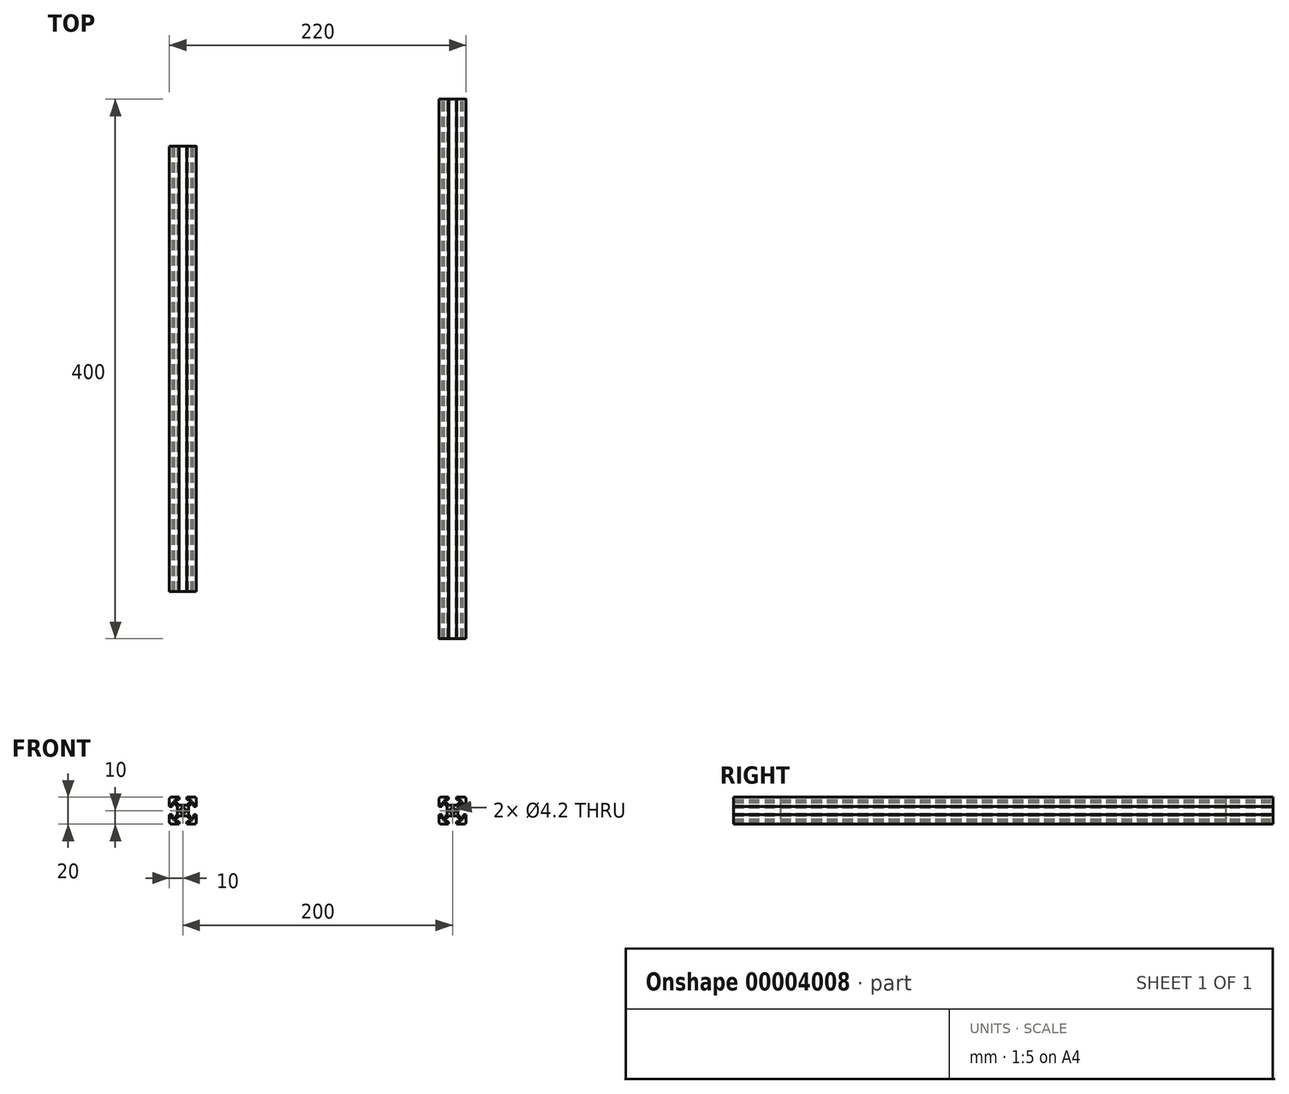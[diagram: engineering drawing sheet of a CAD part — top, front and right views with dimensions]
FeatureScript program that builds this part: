
annotation { "Feature Type Name" : "Feature", "Feature Type Description" : "" }
export const myFeature = defineFeature(function(context is Context, id is Id, definition is map)
    precondition{}
    {
        {
            var Q0;
            Q0=qCreatedBy(makeId("Front.planeOp"),FACE);
            var sketch = newSketch(context, id + "F0", { "sketchPlane" : qUnion([Q0])});
            skLineSegment(sketch, "E0", {"start": v(0, 0) * mm, "end": v(0, 4) * mm, "construction": true});
            skLineSegment(sketch, "E1", {"start": v(-2.94, 4) * mm, "end": v(2.94, 4) * mm});
            skLineSegment(sketch, "E2", {"start": v(0, 0) * mm, "end": v(10, 10) * mm, "construction": true});
            skLineSegment(sketch, "E3", {"start": v(10, 10) * mm, "end": v(-10, 10) * mm, "construction": true});
            skLineSegment(sketch, "E4", {"start": v(-10, 10) * mm, "end": v(0, 0) * mm, "construction": true});
            skLineSegment(sketch, "E5", {"start": v(-10, 10) * mm, "end": v(-3, 10) * mm});
            skLineSegment(sketch, "E6", {"start": v(-3, 10) * mm, "end": v(-3, 8) * mm});
            skLineSegment(sketch, "E7", {"start": v(-3, 8) * mm, "end": v(-6, 8) * mm});
            skLineSegment(sketch, "E8", {"start": v(-6, 8) * mm, "end": v(-6, 7.06) * mm});
            skLineSegment(sketch, "E9", {"start": v(-6, 7.06) * mm, "end": v(-2.94, 4) * mm});
            skLineSegment(sketch, "E10", {"start": v(2.94, 4) * mm, "end": v(6, 7.06) * mm});
            skLineSegment(sketch, "E11", {"start": v(6, 7.06) * mm, "end": v(6, 8) * mm});
            skLineSegment(sketch, "E12", {"start": v(6, 8) * mm, "end": v(3, 8) * mm});
            skLineSegment(sketch, "E13", {"start": v(3, 8) * mm, "end": v(3, 10) * mm});
            skLineSegment(sketch, "E14", {"start": v(3, 10) * mm, "end": v(10, 10) * mm});
            skLineSegment(sketch, "E15.0.MirrorCS", {"start": v(-10, -3) * mm, "end": v(-10, -10) * mm});
            skLineSegment(sketch, "E15.1.MirrorCS", {"start": v(-7.06, -6) * mm, "end": v(-8, -6) * mm});
            skLineSegment(sketch, "E15.2.MirrorCS", {"start": v(-8, -6) * mm, "end": v(-8, -3) * mm});
            skLineSegment(sketch, "E15.3.MirrorCS", {"start": v(-8, -3) * mm, "end": v(-10, -3) * mm});
            skLineSegment(sketch, "E15.4.MirrorCS", {"start": v(-10, 10) * mm, "end": v(-10, 3) * mm});
            skLineSegment(sketch, "E15.5.MirrorCS", {"start": v(-10, 3) * mm, "end": v(-8, 3) * mm});
            skLineSegment(sketch, "E15.6.MirrorCS", {"start": v(-8, 3) * mm, "end": v(-8, 6) * mm});
            skLineSegment(sketch, "E15.7.MirrorCS", {"start": v(-8, 6) * mm, "end": v(-7.06, 6) * mm});
            skLineSegment(sketch, "E15.8.MirrorCS", {"start": v(-7.06, 6) * mm, "end": v(-4, 2.94) * mm});
            skLineSegment(sketch, "E15.9.MirrorCS", {"start": v(-4, -2.94) * mm, "end": v(-7.06, -6) * mm});
            skLineSegment(sketch, "E15.10.MirrorCS", {"start": v(-4, 2.94) * mm, "end": v(-4, -2.94) * mm});
            skLineSegment(sketch, "E16", {"start": v(-10, -10) * mm, "end": v(0, 0) * mm, "construction": true});
            skLineSegment(sketch, "E17", {"start": v(-10, 10) * mm, "end": v(-10, -10) * mm, "construction": true});
            skLineSegment(sketch, "E18.0.MirrorCS", {"start": v(10, 3) * mm, "end": v(10, 10) * mm});
            skLineSegment(sketch, "E18.1.MirrorCS", {"start": v(8, 3) * mm, "end": v(10, 3) * mm});
            skLineSegment(sketch, "E18.2.MirrorCS", {"start": v(8, 6) * mm, "end": v(8, 3) * mm});
            skLineSegment(sketch, "E18.3.MirrorCS", {"start": v(7.06, 6) * mm, "end": v(8, 6) * mm});
            skLineSegment(sketch, "E18.4.MirrorCS", {"start": v(4, 2.94) * mm, "end": v(7.06, 6) * mm});
            skLineSegment(sketch, "E18.5.MirrorCS", {"start": v(4, -2.94) * mm, "end": v(4, 2.94) * mm});
            skLineSegment(sketch, "E18.6.MirrorCS", {"start": v(7.06, -6) * mm, "end": v(4, -2.94) * mm});
            skLineSegment(sketch, "E18.7.MirrorCS", {"start": v(8, -6) * mm, "end": v(7.06, -6) * mm});
            skLineSegment(sketch, "E18.8.MirrorCS", {"start": v(8, -3) * mm, "end": v(8, -6) * mm});
            skLineSegment(sketch, "E18.9.MirrorCS", {"start": v(10, -3) * mm, "end": v(8, -3) * mm});
            skLineSegment(sketch, "E18.10.MirrorCS", {"start": v(10, -10) * mm, "end": v(10, -3) * mm});
            skLineSegment(sketch, "E18.11.MirrorCS", {"start": v(10, -10) * mm, "end": v(3, -10) * mm});
            skLineSegment(sketch, "E18.12.MirrorCS", {"start": v(3, -10) * mm, "end": v(3, -8) * mm});
            skLineSegment(sketch, "E18.13.MirrorCS", {"start": v(3, -8) * mm, "end": v(6, -8) * mm});
            skLineSegment(sketch, "E18.14.MirrorCS", {"start": v(6, -8) * mm, "end": v(6, -7.06) * mm});
            skLineSegment(sketch, "E18.15.MirrorCS", {"start": v(6, -7.06) * mm, "end": v(2.94, -4) * mm});
            skLineSegment(sketch, "E18.16.MirrorCS", {"start": v(2.94, -4) * mm, "end": v(-2.94, -4) * mm});
            skLineSegment(sketch, "E18.17.MirrorCS", {"start": v(-2.94, -4) * mm, "end": v(-6, -7.06) * mm});
            skLineSegment(sketch, "E18.18.MirrorCS", {"start": v(-6, -7.06) * mm, "end": v(-6, -8) * mm});
            skLineSegment(sketch, "E18.19.MirrorCS", {"start": v(-6, -8) * mm, "end": v(-3, -8) * mm});
            skLineSegment(sketch, "E18.20.MirrorCS", {"start": v(-3, -10) * mm, "end": v(-10, -10) * mm});
            skLineSegment(sketch, "E18.21.MirrorCS", {"start": v(-3, -8) * mm, "end": v(-3, -10) * mm});
            skLineSegment(sketch, "E19", {"start": v(0, 0) * mm, "end": v(10, -10) * mm, "construction": true});
            skLineSegment(sketch, "E20", {"start": v(10, -10) * mm, "end": v(-10, -10) * mm, "construction": true});
            skLineSegment(sketch, "E21", {"start": v(10, 10) * mm, "end": v(10, -10) * mm, "construction": true});
            skCircle(sketch, "E22", {"center": v(0, 0) * mm, "radius": 2.1 * mm});
            skSolve(sketch);
        }
        {
            var Q0;
            Q0=makeQuery(id+"F0.imprint","IMPRINT",FACE,{"disambiguationData":[TD([[makeQuery(id+"F0.imprint","IMPRINT",EDGE,{"derivedFrom":sQuery(id+"F0.wireOp",EDGE,"E1")}),-1.0]])]});
            extrude(context, id + "F1", {"entities" : qUnion([Q0]), "depth" : 400 * mm, "symmetric" : true});
        }
        {
            var Q0;
            Q0=makeQuery(id+"F1.opExtrude","SWEPT_EDGE",EDGE,{"disambiguationData":[OSD([sQuery(id+"F0.wireOp",EDGE,"E18.10.MirrorCS"),sQuery(id+"F0.wireOp",EDGE,"E18.11.MirrorCS")])]});
            var Q1;
            Q1=makeQuery(id+"F1.opExtrude","SWEPT_EDGE",EDGE,{"disambiguationData":[OSD([sQuery(id+"F0.wireOp",EDGE,"E14"),sQuery(id+"F0.wireOp",EDGE,"E18.0.MirrorCS")])]});
            var Q2;
            Q2=makeQuery(id+"F1.opExtrude","SWEPT_EDGE",EDGE,{"disambiguationData":[OSD([sQuery(id+"F0.wireOp",EDGE,"E5"),sQuery(id+"F0.wireOp",EDGE,"E15.4.MirrorCS")])]});
            var Q3;
            Q3=makeQuery(id+"F1.opExtrude","SWEPT_EDGE",EDGE,{"disambiguationData":[OSD([sQuery(id+"F0.wireOp",EDGE,"E15.0.MirrorCS"),sQuery(id+"F0.wireOp",EDGE,"E18.20.MirrorCS")])]});
            fillet(context, id + "F2", {"entities" : qUnion([Q0, Q1, Q2, Q3]), "radius" : 1.5 * mm, "tangentPropagation" : true, "allowEdgeOverflow" : false});
        }
        {
            var Q0;
            Q0=makeQuery(id+"F1.opExtrude","SWEPT_BODY",BODY,{"disambiguationData":[OSD([sQuery(id+"F0.wireOp",EDGE,"E1"),sQuery(id+"F0.wireOp",EDGE,"E5"),sQuery(id+"F0.wireOp",EDGE,"E6"),sQuery(id+"F0.wireOp",EDGE,"E7"),sQuery(id+"F0.wireOp",EDGE,"E8"),sQuery(id+"F0.wireOp",EDGE,"E9"),sQuery(id+"F0.wireOp",EDGE,"E10"),sQuery(id+"F0.wireOp",EDGE,"E11"),sQuery(id+"F0.wireOp",EDGE,"E12"),sQuery(id+"F0.wireOp",EDGE,"E13"),sQuery(id+"F0.wireOp",EDGE,"E14"),sQuery(id+"F0.wireOp",EDGE,"E15.0.MirrorCS"),sQuery(id+"F0.wireOp",EDGE,"E15.1.MirrorCS"),sQuery(id+"F0.wireOp",EDGE,"E15.2.MirrorCS"),sQuery(id+"F0.wireOp",EDGE,"E15.3.MirrorCS"),sQuery(id+"F0.wireOp",EDGE,"E15.4.MirrorCS"),sQuery(id+"F0.wireOp",EDGE,"E15.5.MirrorCS"),sQuery(id+"F0.wireOp",EDGE,"E15.6.MirrorCS"),sQuery(id+"F0.wireOp",EDGE,"E15.7.MirrorCS"),sQuery(id+"F0.wireOp",EDGE,"E15.8.MirrorCS"),sQuery(id+"F0.wireOp",EDGE,"E15.9.MirrorCS"),sQuery(id+"F0.wireOp",EDGE,"E15.10.MirrorCS"),sQuery(id+"F0.wireOp",EDGE,"E18.0.MirrorCS"),sQuery(id+"F0.wireOp",EDGE,"E18.1.MirrorCS"),sQuery(id+"F0.wireOp",EDGE,"E18.2.MirrorCS"),sQuery(id+"F0.wireOp",EDGE,"E18.3.MirrorCS"),sQuery(id+"F0.wireOp",EDGE,"E18.4.MirrorCS"),sQuery(id+"F0.wireOp",EDGE,"E18.5.MirrorCS"),sQuery(id+"F0.wireOp",EDGE,"E18.6.MirrorCS"),sQuery(id+"F0.wireOp",EDGE,"E18.7.MirrorCS"),sQuery(id+"F0.wireOp",EDGE,"E18.8.MirrorCS"),sQuery(id+"F0.wireOp",EDGE,"E18.9.MirrorCS"),sQuery(id+"F0.wireOp",EDGE,"E18.10.MirrorCS"),sQuery(id+"F0.wireOp",EDGE,"E18.11.MirrorCS"),sQuery(id+"F0.wireOp",EDGE,"E18.12.MirrorCS"),sQuery(id+"F0.wireOp",EDGE,"E18.13.MirrorCS"),sQuery(id+"F0.wireOp",EDGE,"E18.14.MirrorCS"),sQuery(id+"F0.wireOp",EDGE,"E18.15.MirrorCS"),sQuery(id+"F0.wireOp",EDGE,"E18.16.MirrorCS"),sQuery(id+"F0.wireOp",EDGE,"E18.17.MirrorCS"),sQuery(id+"F0.wireOp",EDGE,"E18.18.MirrorCS"),sQuery(id+"F0.wireOp",EDGE,"E18.19.MirrorCS"),sQuery(id+"F0.wireOp",EDGE,"E18.20.MirrorCS"),sQuery(id+"F0.wireOp",EDGE,"E18.21.MirrorCS"),sQuery(id+"F0.wireOp",EDGE,"E22")])]});
            transform(context, id + "F3", {"entities" : qUnion([Q0]), "transformType" : TransformType.TRANSLATION_3D, "dx" : 200 * mm, "dy" : 0 * mm, "dz" : 0 * mm, "makeCopy" : false});
        }
        {
            var Q0;
            Q0=makeQuery(id+"F0.imprint","IMPRINT",FACE,{"disambiguationData":[TD([[makeQuery(id+"F0.imprint","IMPRINT",EDGE,{"derivedFrom":sQuery(id+"F0.wireOp",EDGE,"E1")}),-1.0]])]});
            extrude(context, id + "F4", {"entities" : qUnion([Q0]), "depth" : 330 * mm, "symmetric" : true});
        }
        {
            var Q0;
            Q0=makeQuery(id+"F4.opExtrude","SWEPT_EDGE",EDGE,{"disambiguationData":[OSD([sQuery(id+"F0.wireOp",EDGE,"E14"),sQuery(id+"F0.wireOp",EDGE,"E18.0.MirrorCS")])]});
            var Q1;
            Q1=makeQuery(id+"F4.opExtrude","SWEPT_EDGE",EDGE,{"disambiguationData":[OSD([sQuery(id+"F0.wireOp",EDGE,"E5"),sQuery(id+"F0.wireOp",EDGE,"E15.4.MirrorCS")])]});
            var Q2;
            Q2=makeQuery(id+"F4.opExtrude","SWEPT_EDGE",EDGE,{"disambiguationData":[OSD([sQuery(id+"F0.wireOp",EDGE,"E18.10.MirrorCS"),sQuery(id+"F0.wireOp",EDGE,"E18.11.MirrorCS")])]});
            var Q3;
            Q3=makeQuery(id+"F4.opExtrude","SWEPT_EDGE",EDGE,{"disambiguationData":[OSD([sQuery(id+"F0.wireOp",EDGE,"E15.0.MirrorCS"),sQuery(id+"F0.wireOp",EDGE,"E18.20.MirrorCS")])]});
            fillet(context, id + "F5", {"entities" : qUnion([Q0, Q1, Q2, Q3]), "radius" : 1.5 * mm, "tangentPropagation" : true, "allowEdgeOverflow" : false});
        }
    });
